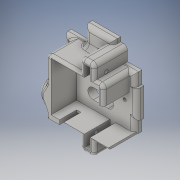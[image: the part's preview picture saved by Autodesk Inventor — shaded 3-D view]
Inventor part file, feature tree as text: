
AUTODESK INVENTOR PART (.ipt)
format: ipt  version: 2016 (Build 200138000, 138)  size: 569,344 bytes
history: native  units: in
note: dims shown in document units (in); Inventor stores cm internally (conversion verified against a paired STEP export)
features: sketch x16, other x3
ambient origin geometry x8: Origin, YZ Plane, XZ Plane, XY Plane, X Axis, Y Axis, Z Axis, Center Point
bodies: Solid1 (feature_tree)
feature tree (19):
  other  "Hip_holder_v2.ipt"
  other  "Solid1::Hip_holder_v2.ipt"
  other  "TaggingFeature1"
  sketch  "Sketch1"  dims[d0=0.3937in]
  sketch  "Sketch12"
  sketch  "Sketch14"
  sketch  "Sketch17"
  sketch  "Sketch18"
  sketch  "Sketch21"
  sketch  "Sketch22"
  sketch  "Sketch23"
  sketch  "Sketch24"
  sketch  "Sketch25"
  sketch  "Sketch26"
  sketch  "Sketch27"
  sketch  "Sketch28"
  sketch  "Sketch29"
  sketch  "Sketch30"
  sketch  "Sketch31"
